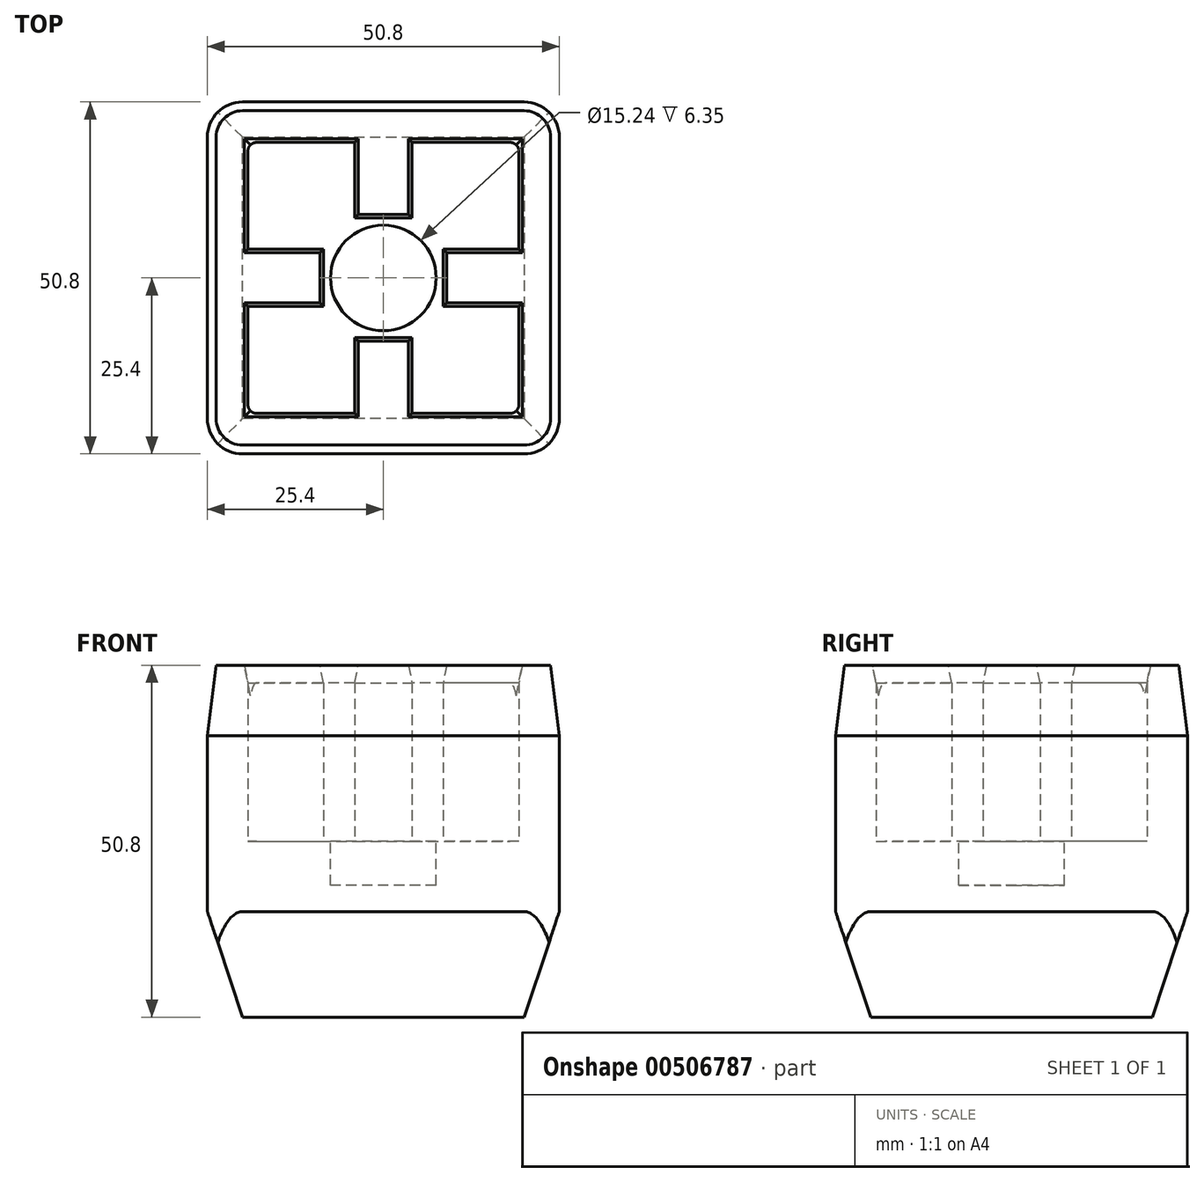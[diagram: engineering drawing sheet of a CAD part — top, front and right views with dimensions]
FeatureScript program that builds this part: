
annotation { "Feature Type Name" : "Feature", "Feature Type Description" : "" }
export const myFeature = defineFeature(function(context is Context, id is Id, definition is map)
    precondition{}
    {
        {
            var Q0;
            Q0=qCreatedBy(makeId("Top.planeOp"),FACE);
            var sketch = newSketch(context, id + "F0", { "sketchPlane" : qUnion([Q0])});
            skLineSegment(sketch, "E0.bottom", {"start": v(-19.56, 19.56) * mm, "end": v(19.56, 19.56) * mm});
            skLineSegment(sketch, "E0.top", {"start": v(-19.56, -19.56) * mm, "end": v(19.56, -19.56) * mm});
            skLineSegment(sketch, "E0.left", {"start": v(-19.56, 19.56) * mm, "end": v(-19.56, -19.56) * mm});
            skLineSegment(sketch, "E0.right", {"start": v(19.56, 19.56) * mm, "end": v(19.56, -19.56) * mm});
            skLineSegment(sketch, "E1.bottom", {"start": v(-25.4, 25.4) * mm, "end": v(25.4, 25.4) * mm});
            skLineSegment(sketch, "E1.top", {"start": v(-25.4, -25.4) * mm, "end": v(25.4, -25.4) * mm});
            skLineSegment(sketch, "E1.left", {"start": v(-25.4, 25.4) * mm, "end": v(-25.4, -25.4) * mm});
            skLineSegment(sketch, "E1.right", {"start": v(25.4, 25.4) * mm, "end": v(25.4, -25.4) * mm});
            skSolve(sketch);
        }
        {
            var Q0;
            Q0=makeQuery(id+"F0.imprint","IMPRINT",FACE,{"disambiguationData":[TD([[makeQuery(id+"F0.imprint","IMPRINT",EDGE,{"derivedFrom":sQuery(id+"F0.wireOp",EDGE,"E0.bottom")}),1.0]])]});
            extrude(context, id + "F1", {"entities" : qUnion([Q0]), "depth" : 25.4 * mm});
        }
        {
            var Q0;
            Q0=makeQuery(id+"F1.opExtrude","CAP_FACE",FACE,{"disambiguationData":[OSD([sQuery(id+"F0.wireOp",EDGE,"E0.bottom"),sQuery(id+"F0.wireOp",EDGE,"E0.top"),sQuery(id+"F0.wireOp",EDGE,"E0.left"),sQuery(id+"F0.wireOp",EDGE,"E0.right"),sQuery(id+"F0.wireOp",EDGE,"E1.bottom"),sQuery(id+"F0.wireOp",EDGE,"E1.top"),sQuery(id+"F0.wireOp",EDGE,"E1.left"),sQuery(id+"F0.wireOp",EDGE,"E1.right")])],"isStart":true});
            var sketch = newSketch(context, id + "F2", { "sketchPlane" : qUnion([Q0])});
            skLineSegment(sketch, "E2.bottom", {"start": v(-25.4, 25.4) * mm, "end": v(25.4, 25.4) * mm});
            skLineSegment(sketch, "E2.top", {"start": v(-25.4, -25.4) * mm, "end": v(25.4, -25.4) * mm});
            skLineSegment(sketch, "E2.left", {"start": v(-25.4, 25.4) * mm, "end": v(-25.4, -25.4) * mm});
            skLineSegment(sketch, "E2.right", {"start": v(25.4, 25.4) * mm, "end": v(25.4, -25.4) * mm});
            skSolve(sketch);
        }
        {
            var Q0;
            Q0 = qSketchRegion(id + "F2", true);
            extrude(context, id + "F3", {"entities" : qUnion([Q0]), "operationType" : NewBodyOperationType.ADD, "depth" : 25.4 * mm});
        }
        {
            var Q0;
            Q0=makeQuery(id+"F3.opExtrude","CAP_FACE",FACE,{"disambiguationData":[OSD([sQuery(id+"F2.wireOp",EDGE,"E2.bottom"),sQuery(id+"F2.wireOp",EDGE,"E2.top"),sQuery(id+"F2.wireOp",EDGE,"E2.left"),sQuery(id+"F2.wireOp",EDGE,"E2.right")])],"isStart":true});
            var sketch = newSketch(context, id + "F4", { "sketchPlane" : qUnion([Q0])});
            skLineSegment(sketch, "E3.bottom", {"start": v(-4.13, -19.56) * mm, "end": v(4.13, -19.56) * mm});
            skLineSegment(sketch, "E3.top", {"start": v(-4.13, -8.64) * mm, "end": v(4.13, -8.64) * mm});
            skLineSegment(sketch, "E3.left", {"start": v(-4.13, -19.56) * mm, "end": v(-4.13, -8.64) * mm});
            skLineSegment(sketch, "E3.right", {"start": v(4.13, -19.56) * mm, "end": v(4.13, -8.64) * mm});
            skLineSegment(sketch, "E4.1.0", {"start": v(8.64, -4.13) * mm, "end": v(8.64, 4.13) * mm});
            skLineSegment(sketch, "E4.1.1", {"start": v(19.56, -4.13) * mm, "end": v(8.64, -4.13) * mm});
            skLineSegment(sketch, "E4.1.2", {"start": v(19.56, 4.13) * mm, "end": v(8.64, 4.13) * mm});
            skLineSegment(sketch, "E4.2.0", {"start": v(4.13, 8.64) * mm, "end": v(-4.13, 8.64) * mm});
            skLineSegment(sketch, "E4.2.1", {"start": v(4.13, 19.56) * mm, "end": v(4.13, 8.64) * mm});
            skLineSegment(sketch, "E4.2.2", {"start": v(-4.13, 19.56) * mm, "end": v(-4.13, 8.64) * mm});
            skLineSegment(sketch, "E4.3.0", {"start": v(-8.64, 4.13) * mm, "end": v(-8.64, -4.13) * mm});
            skLineSegment(sketch, "E4.3.1", {"start": v(-19.56, 4.13) * mm, "end": v(-8.64, 4.13) * mm});
            skLineSegment(sketch, "E4.3.2", {"start": v(-19.56, -4.13) * mm, "end": v(-8.64, -4.13) * mm});
            skPoint(sketch, "E4.center", {"position": v(0, 0) * mm});
            skSolve(sketch);
        }
        {
            var Q0;
            Q0=makeQuery(id+"F4.imprint","IMPRINT",FACE,{"disambiguationData":[TD([[makeQuery(id+"F4.imprint","IMPRINT",EDGE,{"derivedFrom":sQuery(id+"F4.wireOp",EDGE,"E4.3.0")}),-1.0]])]});
            var Q1;
            Q1=makeQuery(id+"F4.imprint","IMPRINT",FACE,{"disambiguationData":[TD([[makeQuery(id+"F4.imprint","IMPRINT",EDGE,{"derivedFrom":sQuery(id+"F4.wireOp",EDGE,"E4.2.0")}),-1.0]])]});
            var Q2;
            Q2=makeQuery(id+"F4.imprint","IMPRINT",FACE,{"disambiguationData":[TD([[makeQuery(id+"F4.imprint","IMPRINT",EDGE,{"derivedFrom":sQuery(id+"F4.wireOp",EDGE,"E4.1.0")}),-1.0]])]});
            var Q3;
            Q3=makeQuery(id+"F4.imprint","IMPRINT",FACE,{"disambiguationData":[TD([[makeQuery(id+"F4.imprint","IMPRINT",EDGE,{"derivedFrom":sQuery(id+"F4.wireOp",EDGE,"E3.bottom")}),1.0]])]});
            extrude(context, id + "F5", {"entities" : qUnion([Q0, Q1, Q2, Q3]), "operationType" : NewBodyOperationType.ADD, "depth" : 25.4 * mm});
        }
        {
            var Q0;
            Q0=makeQuery(id+"F3.opExtrude","CAP_FACE",FACE,{"disambiguationData":[OSD([sQuery(id+"F2.wireOp",EDGE,"E2.bottom"),sQuery(id+"F2.wireOp",EDGE,"E2.top"),sQuery(id+"F2.wireOp",EDGE,"E2.left"),sQuery(id+"F2.wireOp",EDGE,"E2.right")])],"isStart":true});
            var sketch = newSketch(context, id + "F6", { "sketchPlane" : qUnion([Q0])});
            skCircle(sketch, "E5", {"center": v(0, 0) * mm, "radius": 7.62 * mm});
            skSolve(sketch);
        }
        {
            var Q0;
            Q0 = qSketchRegion(id + "F6", true);
            extrude(context, id + "F7", {"entities" : qUnion([Q0]), "operationType" : NewBodyOperationType.REMOVE, "oppositeDirection" : true, "depth" : 6.35 * mm});
        }
        {
            var Q0;
            Q0=makeQuery(id+"F3.opExtrude","CAP_EDGE",EDGE,{"disambiguationData":[OSD([sQuery(id+"F2.wireOp",EDGE,"E2.right")])],"isStart":false});
            var Q1;
            Q1=makeQuery(id+"F3.opExtrude","CAP_EDGE",EDGE,{"disambiguationData":[OSD([sQuery(id+"F2.wireOp",EDGE,"E2.bottom")])],"isStart":false});
            var Q2;
            Q2=makeQuery(id+"F3.opExtrude","CAP_EDGE",EDGE,{"disambiguationData":[OSD([sQuery(id+"F2.wireOp",EDGE,"E2.left")])],"isStart":false});
            var Q3;
            Q3=makeQuery(id+"F3.opExtrude","CAP_EDGE",EDGE,{"disambiguationData":[OSD([sQuery(id+"F2.wireOp",EDGE,"E2.top")])],"isStart":false});
            chamfer(context, id + "F8", {"entities" : qUnion([Q0, Q1, Q2, Q3]), "chamferType" : ChamferType.TWO_OFFSETS, "width1" : 5.08 * mm, "oppositeDirection" : false, "width2" : 15.24 * mm, "tangentPropagation" : true});
        }
        {
            var Q0;
            Q0=makeQuery(id+"F3.boolean.opBoolean","MERGE",EDGE,{"derivedFrom":[makeQuery(id+"F1.opExtrude","SWEPT_EDGE",EDGE,{"disambiguationData":[OSD([sQuery(id+"F0.wireOp",EDGE,"E1.top"),sQuery(id+"F0.wireOp",EDGE,"E1.right")])]}),makeQuery(id+"F3.opExtrude","SWEPT_EDGE",EDGE,{"disambiguationData":[OSD([sQuery(id+"F2.wireOp",EDGE,"E2.bottom"),sQuery(id+"F2.wireOp",EDGE,"E2.right")])]})]});
            var Q1;
            Q1=makeQuery(id+"F3.boolean.opBoolean","MERGE",EDGE,{"derivedFrom":[makeQuery(id+"F1.opExtrude","SWEPT_EDGE",EDGE,{"disambiguationData":[OSD([sQuery(id+"F0.wireOp",EDGE,"E1.bottom"),sQuery(id+"F0.wireOp",EDGE,"E1.right")])]}),makeQuery(id+"F3.opExtrude","SWEPT_EDGE",EDGE,{"disambiguationData":[OSD([sQuery(id+"F2.wireOp",EDGE,"E2.top"),sQuery(id+"F2.wireOp",EDGE,"E2.right")])]})]});
            var Q2;
            Q2=makeQuery(id+"F3.boolean.opBoolean","MERGE",EDGE,{"derivedFrom":[makeQuery(id+"F1.opExtrude","SWEPT_EDGE",EDGE,{"disambiguationData":[OSD([sQuery(id+"F0.wireOp",EDGE,"E1.bottom"),sQuery(id+"F0.wireOp",EDGE,"E1.left")])]}),makeQuery(id+"F3.opExtrude","SWEPT_EDGE",EDGE,{"disambiguationData":[OSD([sQuery(id+"F2.wireOp",EDGE,"E2.top"),sQuery(id+"F2.wireOp",EDGE,"E2.left")])]})]});
            var Q3;
            Q3=makeQuery(id+"F3.boolean.opBoolean","MERGE",EDGE,{"derivedFrom":[makeQuery(id+"F1.opExtrude","SWEPT_EDGE",EDGE,{"disambiguationData":[OSD([sQuery(id+"F0.wireOp",EDGE,"E1.top"),sQuery(id+"F0.wireOp",EDGE,"E1.left")])]}),makeQuery(id+"F3.opExtrude","SWEPT_EDGE",EDGE,{"disambiguationData":[OSD([sQuery(id+"F2.wireOp",EDGE,"E2.bottom"),sQuery(id+"F2.wireOp",EDGE,"E2.left")])]})]});
            fillet(context, id + "F9", {"entities" : qUnion([Q0, Q1, Q2, Q3]), "radius" : 5.08 * mm, "tangentPropagation" : true, "allowEdgeOverflow" : false});
        }
        {
            var Q0;
            Q0=makeQuery(id+"F1.opExtrude","CAP_EDGE",EDGE,{"disambiguationData":[OSD([sQuery(id+"F0.wireOp",EDGE,"E1.bottom")])],"isStart":false});
            chamfer(context, id + "F10", {"entities" : qUnion([Q0]), "chamferType" : ChamferType.TWO_OFFSETS, "width1" : 10.16 * mm, "oppositeDirection" : false, "width2" : 1.27 * mm, "tangentPropagation" : true});
        }
        {
            var Q0;
            {var subQ2=sQuery(id+"F0.wireOp",EDGE,"E0.right");var subQ3=sQuery(id+"F0.wireOp",EDGE,"E0.top");Q0=makeQuery(id+"F5.boolean.opBoolean","SPLIT",EDGE,{"disambiguationData":[TD([makeQuery(id+"F1.opExtrude","SWEPT_FACE",FACE,{"disambiguationData":[OSD([subQ2])]})])],"derivedFrom":makeQuery(id+"F1.opExtrude","CAP_EDGE",EDGE,{"disambiguationData":[OSD([subQ3])],"isStart":false})});}
            var Q1;
            Q1=makeQuery(id+"F5.opExtrude","CAP_EDGE",EDGE,{"disambiguationData":[OSD([sQuery(id+"F4.wireOp",EDGE,"E3.right")])],"isStart":false});
            var Q2;
            Q2=makeQuery(id+"F5.opExtrude","CAP_EDGE",EDGE,{"disambiguationData":[OSD([sQuery(id+"F4.wireOp",EDGE,"E3.top")])],"isStart":false});
            var Q3;
            Q3=makeQuery(id+"F5.opExtrude","CAP_EDGE",EDGE,{"disambiguationData":[OSD([sQuery(id+"F4.wireOp",EDGE,"E3.left")])],"isStart":false});
            var Q4;
            {var subQ2=sQuery(id+"F0.wireOp",EDGE,"E0.left");var subQ3=sQuery(id+"F0.wireOp",EDGE,"E0.top");Q4=makeQuery(id+"F5.boolean.opBoolean","SPLIT",EDGE,{"disambiguationData":[TD([makeQuery(id+"F1.opExtrude","SWEPT_FACE",FACE,{"disambiguationData":[OSD([subQ2])]})])],"derivedFrom":makeQuery(id+"F1.opExtrude","CAP_EDGE",EDGE,{"disambiguationData":[OSD([subQ3])],"isStart":false})});}
            var Q5;
            {var subQ1=sQuery(id+"F0.wireOp",EDGE,"E0.left");var subQ3=sQuery(id+"F0.wireOp",EDGE,"E0.top");Q5=makeQuery(id+"F5.boolean.opBoolean","SPLIT",EDGE,{"disambiguationData":[TD([makeQuery(id+"F1.opExtrude","SWEPT_FACE",FACE,{"disambiguationData":[OSD([subQ3])]})])],"derivedFrom":makeQuery(id+"F1.opExtrude","CAP_EDGE",EDGE,{"disambiguationData":[OSD([subQ1])],"isStart":false})});}
            var Q6;
            Q6=makeQuery(id+"F5.opExtrude","CAP_EDGE",EDGE,{"disambiguationData":[OSD([sQuery(id+"F4.wireOp",EDGE,"E4.3.2")])],"isStart":false});
            var Q7;
            Q7=makeQuery(id+"F5.opExtrude","CAP_EDGE",EDGE,{"disambiguationData":[OSD([sQuery(id+"F4.wireOp",EDGE,"E4.3.0")])],"isStart":false});
            var Q8;
            Q8=makeQuery(id+"F5.opExtrude","CAP_EDGE",EDGE,{"disambiguationData":[OSD([sQuery(id+"F4.wireOp",EDGE,"E4.3.1")])],"isStart":false});
            var Q9;
            {var subQ0=sQuery(id+"F0.wireOp",EDGE,"E0.bottom");var subQ1=sQuery(id+"F0.wireOp",EDGE,"E0.left");Q9=makeQuery(id+"F5.boolean.opBoolean","SPLIT",EDGE,{"disambiguationData":[TD([makeQuery(id+"F1.opExtrude","SWEPT_FACE",FACE,{"disambiguationData":[OSD([subQ0])]})])],"derivedFrom":makeQuery(id+"F1.opExtrude","CAP_EDGE",EDGE,{"disambiguationData":[OSD([subQ1])],"isStart":false})});}
            var Q10;
            {var subQ1=sQuery(id+"F0.wireOp",EDGE,"E0.bottom");var subQ2=sQuery(id+"F0.wireOp",EDGE,"E0.left");Q10=makeQuery(id+"F5.boolean.opBoolean","SPLIT",EDGE,{"disambiguationData":[TD([makeQuery(id+"F1.opExtrude","SWEPT_FACE",FACE,{"disambiguationData":[OSD([subQ2])]})])],"derivedFrom":makeQuery(id+"F1.opExtrude","CAP_EDGE",EDGE,{"disambiguationData":[OSD([subQ1])],"isStart":false})});}
            var Q11;
            Q11=makeQuery(id+"F5.opExtrude","CAP_EDGE",EDGE,{"disambiguationData":[OSD([sQuery(id+"F4.wireOp",EDGE,"E4.2.2")])],"isStart":false});
            var Q12;
            Q12=makeQuery(id+"F5.opExtrude","CAP_EDGE",EDGE,{"disambiguationData":[OSD([sQuery(id+"F4.wireOp",EDGE,"E4.2.0")])],"isStart":false});
            var Q13;
            Q13=makeQuery(id+"F5.opExtrude","CAP_EDGE",EDGE,{"disambiguationData":[OSD([sQuery(id+"F4.wireOp",EDGE,"E4.2.1")])],"isStart":false});
            var Q14;
            {var subQ1=sQuery(id+"F0.wireOp",EDGE,"E0.bottom");var subQ2=sQuery(id+"F0.wireOp",EDGE,"E0.right");Q14=makeQuery(id+"F5.boolean.opBoolean","SPLIT",EDGE,{"disambiguationData":[TD([makeQuery(id+"F1.opExtrude","SWEPT_FACE",FACE,{"disambiguationData":[OSD([subQ2])]})])],"derivedFrom":makeQuery(id+"F1.opExtrude","CAP_EDGE",EDGE,{"disambiguationData":[OSD([subQ1])],"isStart":false})});}
            var Q15;
            {var subQ0=sQuery(id+"F0.wireOp",EDGE,"E0.bottom");var subQ1=sQuery(id+"F0.wireOp",EDGE,"E0.right");Q15=makeQuery(id+"F5.boolean.opBoolean","SPLIT",EDGE,{"disambiguationData":[TD([makeQuery(id+"F1.opExtrude","SWEPT_FACE",FACE,{"disambiguationData":[OSD([subQ0])]})])],"derivedFrom":makeQuery(id+"F1.opExtrude","CAP_EDGE",EDGE,{"disambiguationData":[OSD([subQ1])],"isStart":false})});}
            var Q16;
            Q16=makeQuery(id+"F5.opExtrude","CAP_EDGE",EDGE,{"disambiguationData":[OSD([sQuery(id+"F4.wireOp",EDGE,"E4.1.2")])],"isStart":false});
            var Q17;
            Q17=makeQuery(id+"F5.opExtrude","CAP_EDGE",EDGE,{"disambiguationData":[OSD([sQuery(id+"F4.wireOp",EDGE,"E4.1.1")])],"isStart":false});
            var Q18;
            {var subQ1=sQuery(id+"F0.wireOp",EDGE,"E0.right");var subQ2=sQuery(id+"F0.wireOp",EDGE,"E0.top");Q18=makeQuery(id+"F5.boolean.opBoolean","SPLIT",EDGE,{"disambiguationData":[TD([makeQuery(id+"F1.opExtrude","SWEPT_FACE",FACE,{"disambiguationData":[OSD([subQ2])]})])],"derivedFrom":makeQuery(id+"F1.opExtrude","CAP_EDGE",EDGE,{"disambiguationData":[OSD([subQ1])],"isStart":false})});}
            var Q19;
            Q19=makeQuery(id+"F5.opExtrude","CAP_EDGE",EDGE,{"disambiguationData":[OSD([sQuery(id+"F4.wireOp",EDGE,"E4.1.0")])],"isStart":false});
            chamfer(context, id + "F11", {"entities" : qUnion([Q0, Q1, Q2, Q3, Q4, Q5, Q6, Q7, Q8, Q9, Q10, Q11, Q12, Q13, Q14, Q15, Q16, Q17, Q18, Q19]), "chamferType" : ChamferType.TWO_OFFSETS, "width1" : 2.54 * mm, "oppositeDirection" : false, "width2" : 0.5 * mm, "tangentPropagation" : true});
        }
        {
            var Q0;
            Q0=makeQuery(id+"F1.opExtrude","SWEPT_EDGE",EDGE,{"disambiguationData":[OSD([sQuery(id+"F0.wireOp",EDGE,"E0.bottom"),sQuery(id+"F0.wireOp",EDGE,"E0.left")])]});
            var Q1;
            Q1=makeQuery(id+"F1.opExtrude","SWEPT_EDGE",EDGE,{"disambiguationData":[OSD([sQuery(id+"F0.wireOp",EDGE,"E0.bottom"),sQuery(id+"F0.wireOp",EDGE,"E0.right")])]});
            var Q2;
            Q2=makeQuery(id+"F1.opExtrude","SWEPT_EDGE",EDGE,{"disambiguationData":[OSD([sQuery(id+"F0.wireOp",EDGE,"E0.top"),sQuery(id+"F0.wireOp",EDGE,"E0.right")])]});
            var Q3;
            Q3=makeQuery(id+"F1.opExtrude","SWEPT_EDGE",EDGE,{"disambiguationData":[OSD([sQuery(id+"F0.wireOp",EDGE,"E0.top"),sQuery(id+"F0.wireOp",EDGE,"E0.left")])]});
            fillet(context, id + "F12", {"entities" : qUnion([Q0, Q1, Q2, Q3]), "radius" : 1.27 * mm, "tangentPropagation" : true, "allowEdgeOverflow" : false});
        }
    });
